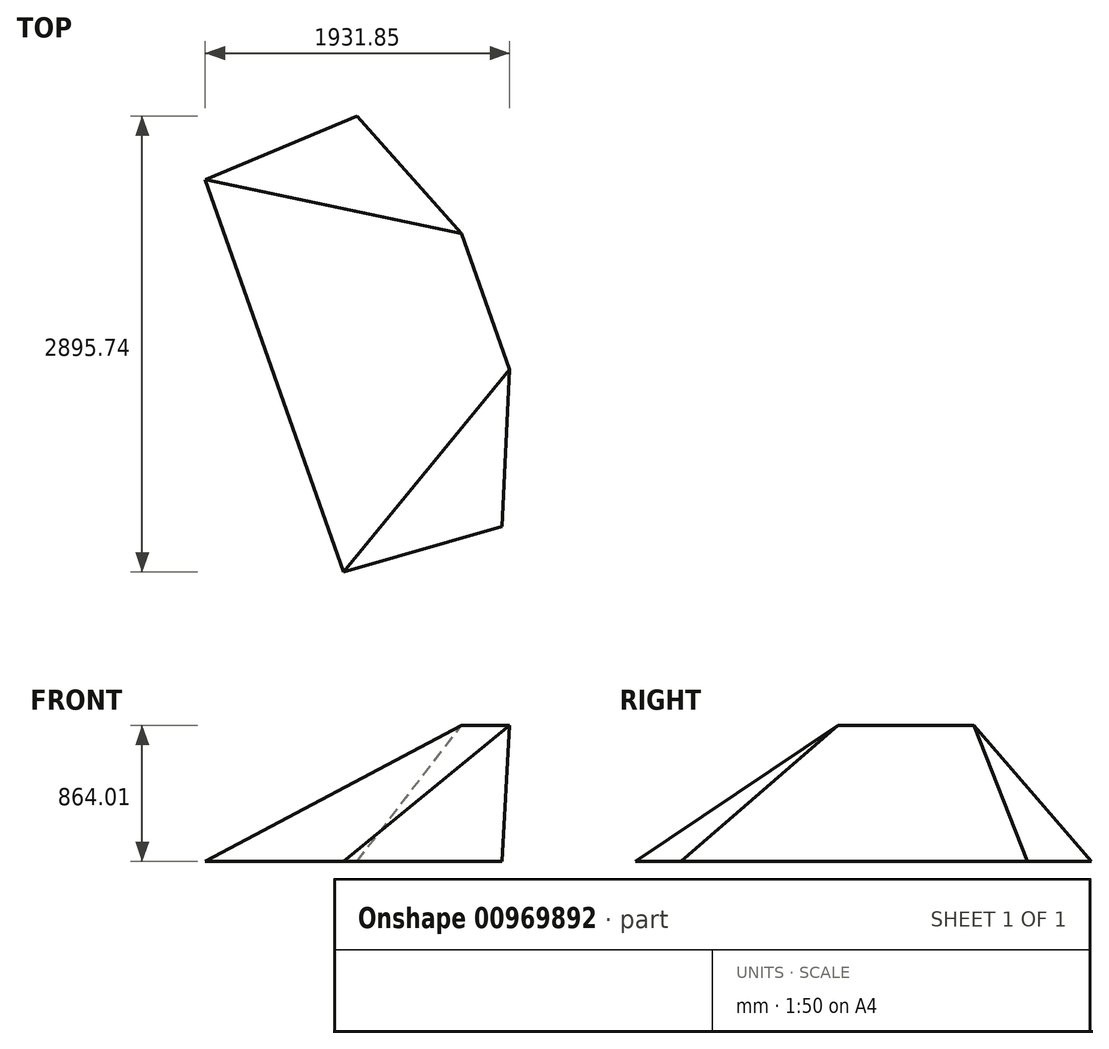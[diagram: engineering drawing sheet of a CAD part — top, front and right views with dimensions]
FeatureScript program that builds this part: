
annotation { "Feature Type Name" : "Feature", "Feature Type Description" : "" }
export const myFeature = defineFeature(function(context is Context, id is Id, definition is map)
    precondition{}
    {
        {
            var Q0;
            Q0=qCreatedBy(makeId("Top.planeOp"),FACE);
            var sketch = newSketch(context, id + "F0", { "sketchPlane" : qUnion([Q0])});
            skLineSegment(sketch, "E0", {"start": v(-304.8, 520.82) * mm, "end": v(304.8, 520.82) * mm});
            skLineSegment(sketch, "E1", {"start": v(0, 520.82) * mm, "end": v(0, -342.78) * mm});
            skSolve(sketch);
        }
        {
            var Q0;
            Q0=qCreatedBy(makeId("Top.planeOp"),FACE);
            var sketch = newSketch(context, id + "F1", { "sketchPlane" : qUnion([Q0])});
            skLineSegment(sketch, "E2", {"start": v(-304.8, 520.82) * mm, "end": v(0, -342.78) * mm});
            skLineSegment(sketch, "E3", {"start": v(0, -342.78) * mm, "end": v(-1052.55, -1629.33) * mm});
            skLineSegment(sketch, "E4", {"start": v(-1052.55, -1629.33) * mm, "end": v(-1931.73, 861.67) * mm});
            skLineSegment(sketch, "E5", {"start": v(-1931.73, 861.67) * mm, "end": v(-304.8, 520.82) * mm});
            skLineSegment(sketch, "E6", {"start": v(-810.18, -1094.97) * mm, "end": v(-1450.9, 563.57) * mm, "construction": true});
            skLineSegment(sketch, "E7", {"start": v(-1450.9, 563.57) * mm, "end": v(-882.26, 783.25) * mm, "construction": true});
            skLineSegment(sketch, "E8", {"start": v(-882.26, 783.25) * mm, "end": v(-241.54, -875.3) * mm, "construction": true});
            skLineSegment(sketch, "E9", {"start": v(-241.54, -875.3) * mm, "end": v(-810.18, -1094.97) * mm, "construction": true});
            skLineSegment(sketch, "E10", {"start": v(-1931.73, 861.67) * mm, "end": v(-967.69, 1266.36) * mm});
            skLineSegment(sketch, "E11", {"start": v(-967.69, 1266.36) * mm, "end": v(-304.8, 520.82) * mm});
            skLineSegment(sketch, "E12", {"start": v(-1052.55, -1629.33) * mm, "end": v(-48.06, -1339.25) * mm});
            skLineSegment(sketch, "E13", {"start": v(-48.06, -1339.25) * mm, "end": v(0, -342.78) * mm});
            skLineSegment(sketch, "E14", {"start": v(-152.4, 89.02) * mm, "end": v(-1492.14, -383.83) * mm, "construction": true});
            skLineSegment(sketch, "E15", {"start": v(-1450.9, 563.57) * mm, "end": v(-241.54, -875.3) * mm, "construction": true});
            skPoint(sketch, "E16", {"position": v(-846.22, -155.86) * mm});
            skSolve(sketch);
        }
        {
            var Q0;
            Q0=sQuery(id+"F1.wireOp",EDGE,"E14");
            var Q1;
            Q1=qCreatedBy(makeId("Top.planeOp"),FACE);
            cPlane(context, id + "F2", {"entities" : qUnion([Q0, Q1]), "cplaneType" : CPlaneType.LINE_ANGLE, "offset" : 25.4 * mm, "angle" : 90 * degree, "width" : 152.4 * mm, "height" : 152.4 * mm});
        }
        {
            var Q0;
            Q0=qCreatedBy(id+"F2.planeOp",FACE);
            var sketch = newSketch(context, id + "F3", { "sketchPlane" : qUnion([Q0])});
            skLineSegment(sketch, "E17", {"start": v(-1534.82, 0) * mm, "end": v(-114.09, 863.6) * mm});
            skSolve(sketch);
        }
        {
            var Q0;
            Q0=qCreatedBy(id+"F2.planeOp",FACE);
            var Q1;
            Q1=sQuery(id+"F3.wireOp",EDGE,"E17");
            cPlane(context, id + "F4", {"entities" : qUnion([Q0, Q1]), "cplaneType" : CPlaneType.LINE_ANGLE, "offset" : 25.4 * mm, "angle" : 90 * degree, "width" : 152.4 * mm, "height" : 152.4 * mm});
        }
        {
            var Q0;
            Q0=qCreatedBy(id+"F4.planeOp",FACE);
            var sketch = newSketch(context, id + "F5", { "sketchPlane" : qUnion([Q0])});
            skLineSegment(sketch, "E18", {"start": v(-1767.83, 844.56) * mm, "end": v(98.28, 681.72) * mm});
            skLineSegment(sketch, "E19", {"start": v(98.28, 681.72) * mm, "end": v(447.9, -164.73) * mm});
            skLineSegment(sketch, "E20", {"start": v(447.9, -164.73) * mm, "end": v(-759.4, -1596.98) * mm});
            skLineSegment(sketch, "E21", {"start": v(-759.4, -1596.98) * mm, "end": v(-1767.83, 844.56) * mm});
            skLineSegment(sketch, "E22", {"start": v(98.28, 681.72) * mm, "end": v(-316.32, 510.47) * mm, "construction": true});
            skSolve(sketch);
        }
        {
            var Q0;
            Q0=sQuery(id+"F5.wireOp",VERTEX,"E19.end");
            var Q1;
            Q1=sQuery(id+"F1.wireOp",VERTEX,"E3.end");
            var Q2;
            Q2=sQuery(id+"F1.wireOp",VERTEX,"E12.end");
            var Q3;
            Q3=sQuery(id+"F1.wireOp",VERTEX,"E3.end");
            var Q4;
            Q4=sQuery(id+"F1.wireOp",VERTEX,"E12.end");
            var Q5;
            Q5=sQuery(id+"F5.wireOp",VERTEX,"E19.end");
            var Q6;
            Q6=sQuery(id+"F1.wireOp",VERTEX,"E3.end");
            var Q7;
            Q7=sQuery(id+"F1.wireOp",VERTEX,"E12.end");
            var Q8;
            Q8=sQuery(id+"F5.wireOp",VERTEX,"E19.end");
            cPlane(context, id + "F6", {"entities" : qUnion([Q0, Q1, Q2, Q3, Q4, Q5, Q6, Q7, Q8]), "cplaneType" : CPlaneType.THREE_POINT, "offset" : 25.4 * mm, "width" : 152.4 * mm, "height" : 152.4 * mm});
        }
        {
            var Q0;
            Q0=qCreatedBy(id+"F6.planeOp",FACE);
            var sketch = newSketch(context, id + "F7", { "sketchPlane" : qUnion([Q0])});
            skLineSegment(sketch, "E23", {"start": v(-1235.37, 1223.83) * mm, "end": v(-212.78, 1005.94) * mm});
            skLineSegment(sketch, "E24", {"start": v(-212.78, 1005.94) * mm, "end": v(-163.86, -312.65) * mm});
            skLineSegment(sketch, "E25", {"start": v(-163.86, -312.65) * mm, "end": v(-1235.37, 1223.83) * mm});
            skSolve(sketch);
        }
        {
            var Q0;
            Q0=makeQuery(id+"F5.imprint","IMPRINT",FACE,{"disambiguationData":[TD([[makeQuery(id+"F5.imprint","IMPRINT",EDGE,{"derivedFrom":sQuery(id+"F5.wireOp",EDGE,"E18")}),-1.0]])]});
            extrude(context, id + "F8", {"entities" : qUnion([Q0]), "depth" : 0.25 * mm, "offsetDistance" : 25.4 * mm});
        }
        {
            var Q0;
            Q0=makeQuery(id+"F7.imprint","IMPRINT",FACE,{"disambiguationData":[TD([[makeQuery(id+"F7.imprint","IMPRINT",EDGE,{"derivedFrom":sQuery(id+"F7.wireOp",EDGE,"E23")}),-1.0]])]});
            extrude(context, id + "F9", {"entities" : qUnion([Q0]), "depth" : 0.25 * mm, "offsetDistance" : 25.4 * mm});
        }
        {
            var Q0;
            Q0=makeQuery(id+"F9.opExtrude","SWEPT_BODY",BODY,{"disambiguationData":[OSD([sQuery(id+"F7.wireOp",EDGE,"E23"),sQuery(id+"F7.wireOp",EDGE,"E24"),sQuery(id+"F7.wireOp",EDGE,"E25")])]});
            var Q1;
            Q1=qCreatedBy(id+"F2.planeOp",FACE);
            mirror(context, id + "F10", {"entities" : qUnion([Q0]), "mirrorPlane" : qUnion([Q1])});
        }
    });
